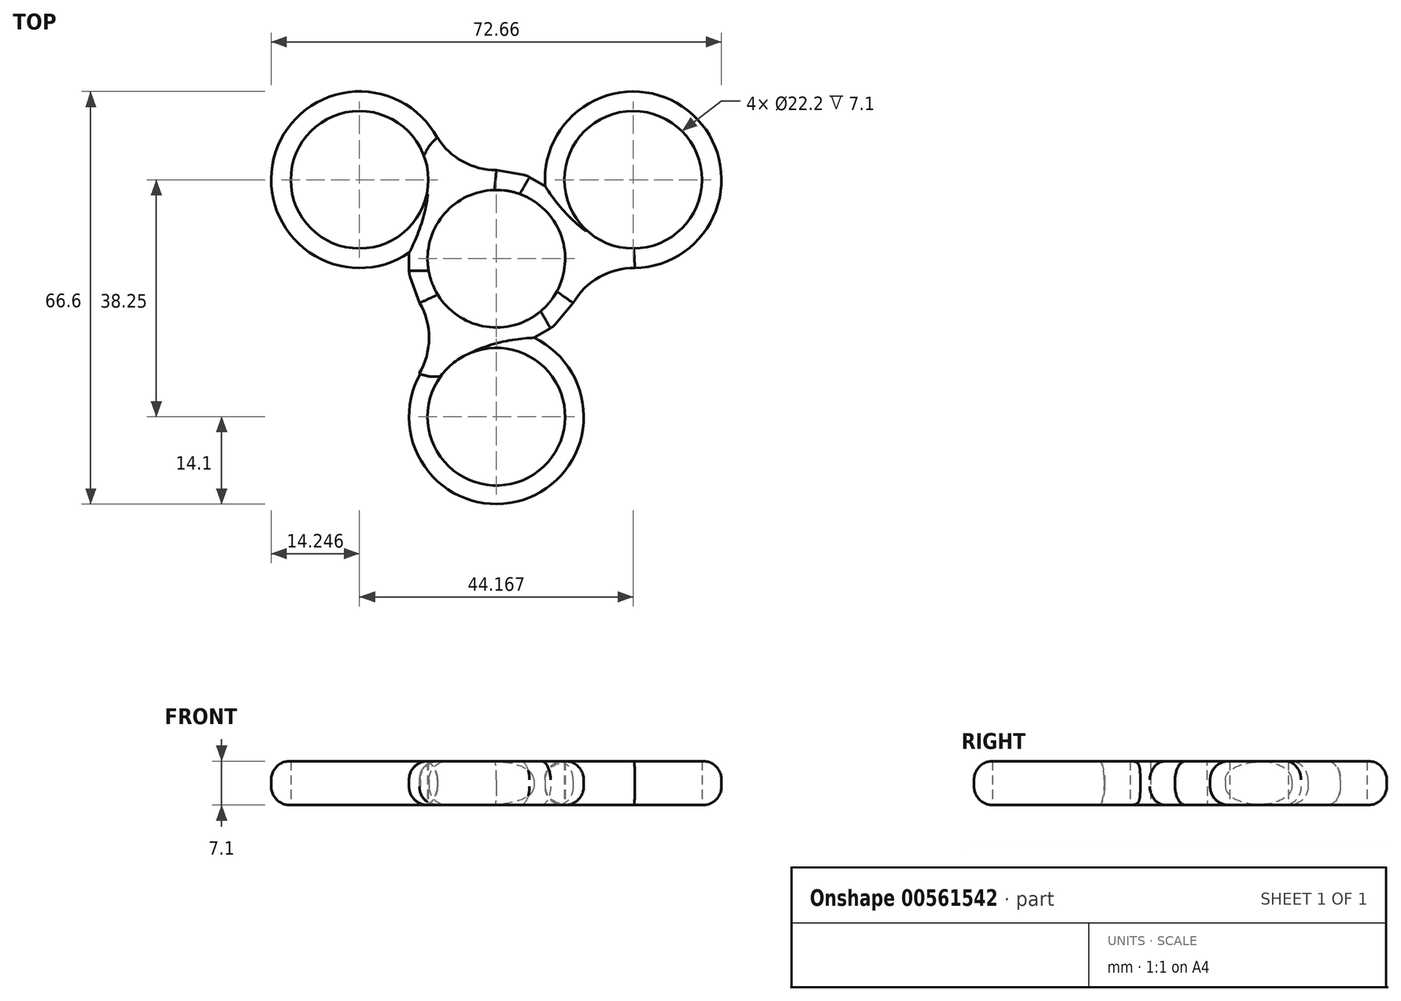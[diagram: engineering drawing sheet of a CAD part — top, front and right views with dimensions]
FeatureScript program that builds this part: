
annotation { "Feature Type Name" : "Feature", "Feature Type Description" : "" }
export const myFeature = defineFeature(function(context is Context, id is Id, definition is map)
    precondition{}
    {
        {
            var Q0;
            Q0=qCreatedBy(makeId("Top.planeOp"),FACE);
            var sketch = newSketch(context, id + "F0", { "sketchPlane" : qUnion([Q0])});
            skCircle(sketch, "E0", {"center": v(0, 0) * mm, "radius": 11.1 * mm});
            skCircle(sketch, "E1.cCircle", {"center": v(0, 0) * mm, "radius": 14.08 * mm, "construction": true});
            skLineSegment(sketch, "E1.0", {"start": v(14.08, 2.48) * mm, "end": v(14.08, -2.48) * mm});
            skLineSegment(sketch, "E1.1", {"start": v(14.08, -2.48) * mm, "end": v(12.38, -7.15) * mm});
            skLineSegment(sketch, "E1.2", {"start": v(12.38, -7.15) * mm, "end": v(9.2, -10.95) * mm});
            skLineSegment(sketch, "E1.3", {"start": v(9.2, -10.95) * mm, "end": v(4.9, -13.44) * mm});
            skLineSegment(sketch, "E1.4", {"start": v(4.9, -13.44) * mm, "end": v(0, -14.3) * mm});
            skLineSegment(sketch, "E1.5", {"start": v(0, -14.3) * mm, "end": v(-4.9, -13.44) * mm});
            skLineSegment(sketch, "E1.6", {"start": v(-4.9, -13.44) * mm, "end": v(-9.2, -10.95) * mm});
            skLineSegment(sketch, "E1.7", {"start": v(-9.2, -10.95) * mm, "end": v(-12.38, -7.15) * mm});
            skLineSegment(sketch, "E1.8", {"start": v(-12.38, -7.15) * mm, "end": v(-14.08, -2.48) * mm});
            skLineSegment(sketch, "E1.9", {"start": v(-14.08, -2.48) * mm, "end": v(-14.08, 2.48) * mm});
            skLineSegment(sketch, "E1.10", {"start": v(-14.08, 2.48) * mm, "end": v(-12.38, 7.15) * mm});
            skLineSegment(sketch, "E1.11", {"start": v(-12.38, 7.15) * mm, "end": v(-9.2, 10.95) * mm});
            skLineSegment(sketch, "E1.12", {"start": v(-9.2, 10.95) * mm, "end": v(-4.9, 13.44) * mm});
            skLineSegment(sketch, "E1.13", {"start": v(-4.9, 13.44) * mm, "end": v(0, 14.3) * mm});
            skLineSegment(sketch, "E1.14", {"start": v(0, 14.3) * mm, "end": v(4.9, 13.44) * mm});
            skLineSegment(sketch, "E1.15", {"start": v(4.9, 13.44) * mm, "end": v(9.2, 10.95) * mm});
            skLineSegment(sketch, "E1.16", {"start": v(9.2, 10.95) * mm, "end": v(12.38, 7.15) * mm});
            skLineSegment(sketch, "E1.17", {"start": v(12.38, 7.15) * mm, "end": v(14.08, 2.48) * mm});
            skPoint(sketch, "E1.0.midPoint", {"position": v(14.08, 0) * mm});
            skLineSegment(sketch, "E2", {"start": v(0, -14.3) * mm, "end": v(0, -25.5) * mm});
            skLineSegment(sketch, "E3", {"start": v(12.38, 7.15) * mm, "end": v(22.08, 12.75) * mm});
            skLineSegment(sketch, "E4", {"start": v(-12.38, 7.15) * mm, "end": v(-22.08, 12.75) * mm});
            skLineSegment(sketch, "E5", {"start": v(0, -25.5) * mm, "end": v(0, -36.25) * mm});
            skLineSegment(sketch, "E6", {"start": v(-22.08, 12.75) * mm, "end": v(-31.44, 18.15) * mm});
            skLineSegment(sketch, "E7", {"start": v(22.08, 12.75) * mm, "end": v(31.92, 18.43) * mm});
            skCircle(sketch, "E8", {"center": v(0, -25.5) * mm, "radius": 11.1 * mm});
            skCircle(sketch, "E9", {"center": v(-22.08, 12.75) * mm, "radius": 11.1 * mm});
            skCircle(sketch, "E10", {"center": v(22.08, 12.75) * mm, "radius": 11.1 * mm});
            skCircle(sketch, "E11.0", {"center": v(-22.08, 12.75) * mm, "radius": 14.25 * mm});
            skCircle(sketch, "E12.0", {"center": v(22.08, 12.75) * mm, "radius": 14.25 * mm});
            skCircle(sketch, "E13.0", {"center": v(0, -25.5) * mm, "radius": 14.1 * mm});
            skLineSegment(sketch, "E14", {"start": v(0, 14.3) * mm, "end": v(0, 25.55) * mm});
            skCircle(sketch, "E15", {"center": v(0, 25.55) * mm, "radius": 11.25 * mm});
            skLineSegment(sketch, "E16", {"start": v(-12.38, -7.15) * mm, "end": v(-22.17, -12.8) * mm});
            skCircle(sketch, "E17", {"center": v(-22.17, -12.8) * mm, "radius": 11.3 * mm});
            skCircle(sketch, "E18", {"center": v(22.17, -12.8) * mm, "radius": 11.3 * mm});
            skCircle(sketch, "E19", {"center": v(15.97, -1.86) * mm, "radius": 6.4 * mm});
            skCircle(sketch, "E20", {"center": v(9.51, -13.38) * mm, "radius": 6.86 * mm});
            skCircle(sketch, "E21", {"center": v(-9.94, -12.85) * mm, "radius": 6.2 * mm});
            skCircle(sketch, "E22", {"center": v(-15.58, -1.28) * mm, "radius": 6.68 * mm});
            skCircle(sketch, "E23", {"center": v(6.28, 14.75) * mm, "radius": 6.3 * mm});
            skPoint(sketch, "E23.second.point", {"position": v(9.78, 20) * mm});
            skPoint(sketch, "E23.third.point", {"position": v(8.83, 9) * mm});
            skCircle(sketch, "E24", {"center": v(-5.99, 14.66) * mm, "radius": 6 * mm});
            skPoint(sketch, "E24.second.point", {"position": v(-9.5, 19.52) * mm});
            skPoint(sketch, "E24.third.point", {"position": v(-8.6, 9.26) * mm});
            skSolve(sketch);
        }
        {
            var Q0;
            {var subQ0=sQuery(id+"F0.wireOp",EDGE,"E20");var subQ1=sQuery(id+"F0.wireOp",EDGE,"E8");var subQ2=makeQuery(id+"F0.imprint","INTERSECT",VERTEX,{"disambiguationData":[OD(1.0)],"derivedFrom":[subQ1,subQ0]});Q0=makeQuery(id+"F0.imprint","IMPRINT",FACE,{"disambiguationData":[TD([[makeQuery(id+"F0.imprint","IMPRINT",EDGE,{"disambiguationData":[TD([[subQ2,1.0]])],"derivedFrom":subQ1}),-1.0]])]});}
            var Q1;
            {var subQ0=sQuery(id+"F0.wireOp",EDGE,"E1.4");var subQ1=sQuery(id+"F0.wireOp",EDGE,"E1.3");var subQ2=makeQuery(id+"F0.imprint","INTERSECT",VERTEX,{"derivedFrom":[subQ1,subQ0]});Q1=makeQuery(id+"F0.imprint","IMPRINT",FACE,{"disambiguationData":[TD([[makeQuery(id+"F0.imprint","IMPRINT",EDGE,{"disambiguationData":[TD([[subQ2,1.0]])],"derivedFrom":subQ1}),1.0]])]});}
            var Q2;
            {var subQ4=sQuery(id+"F0.wireOp",EDGE,"E1.6");var subQ5=sQuery(id+"F0.wireOp",EDGE,"E1.5");var subQ6=makeQuery(id+"F0.imprint","INTERSECT",VERTEX,{"derivedFrom":[subQ5,subQ4]});Q2=makeQuery(id+"F0.imprint","IMPRINT",FACE,{"disambiguationData":[TD([[makeQuery(id+"F0.imprint","IMPRINT",EDGE,{"disambiguationData":[TD([[subQ6,1.0]])],"derivedFrom":subQ5}),1.0]])]});}
            var Q3;
            {var subQ5=sQuery(id+"F0.wireOp",EDGE,"E1.7");Q3=makeQuery(id+"F0.imprint","IMPRINT",FACE,{"disambiguationData":[TD([[makeQuery(id+"F0.imprint","IMPRINT",EDGE,{"derivedFrom":subQ5}),-1.0]])]});}
            var Q4;
            {var subQ9=sQuery(id+"F0.wireOp",EDGE,"E13.0");var subQ11=sQuery(id+"F0.wireOp",EDGE,"E0");var subQ12=makeQuery(id+"F0.imprint","INTERSECT",VERTEX,{"disambiguationData":[OD(0.0)],"derivedFrom":[subQ11,subQ9]});Q4=makeQuery(id+"F0.imprint","IMPRINT",FACE,{"disambiguationData":[TD([[makeQuery(id+"F0.imprint","IMPRINT",EDGE,{"disambiguationData":[TD([[subQ12,-1.0]])],"derivedFrom":subQ11}),-1.0]])]});}
            var Q5;
            {var subQ0=sQuery(id+"F0.wireOp",EDGE,"E1.4");var subQ1=sQuery(id+"F0.wireOp",EDGE,"E1.3");var subQ2=makeQuery(id+"F0.imprint","INTERSECT",VERTEX,{"derivedFrom":[subQ1,subQ0]});Q5=makeQuery(id+"F0.imprint","IMPRINT",FACE,{"disambiguationData":[TD([[makeQuery(id+"F0.imprint","IMPRINT",EDGE,{"disambiguationData":[TD([[subQ2,1.0]])],"derivedFrom":subQ1}),-1.0]])]});}
            var Q6;
            {var subQ0=sQuery(id+"F0.wireOp",EDGE,"E1.6");var subQ1=sQuery(id+"F0.wireOp",EDGE,"E1.5");var subQ2=makeQuery(id+"F0.imprint","INTERSECT",VERTEX,{"derivedFrom":[subQ1,subQ0]});Q6=makeQuery(id+"F0.imprint","IMPRINT",FACE,{"disambiguationData":[TD([[makeQuery(id+"F0.imprint","IMPRINT",EDGE,{"disambiguationData":[TD([[subQ2,1.0]])],"derivedFrom":subQ1}),-1.0]])]});}
            var Q7;
            {var subQ0=sQuery(id+"F0.wireOp",EDGE,"E8");var subQ1=sQuery(id+"F0.wireOp",EDGE,"E1.5");var subQ2=makeQuery(id+"F0.imprint","INTERSECT",VERTEX,{"derivedFrom":[subQ1,subQ0]});Q7=makeQuery(id+"F0.imprint","IMPRINT",FACE,{"disambiguationData":[TD([[makeQuery(id+"F0.imprint","IMPRINT",EDGE,{"disambiguationData":[TD([[subQ2,-1.0]])],"derivedFrom":subQ1}),1.0]])]});}
            var Q8;
            {var subQ0=sQuery(id+"F0.wireOp",EDGE,"E20");var subQ1=sQuery(id+"F0.wireOp",EDGE,"E1.4");var subQ2=makeQuery(id+"F0.imprint","INTERSECT",VERTEX,{"derivedFrom":[subQ1,subQ0]});Q8=makeQuery(id+"F0.imprint","IMPRINT",FACE,{"disambiguationData":[TD([[makeQuery(id+"F0.imprint","IMPRINT",EDGE,{"disambiguationData":[TD([[subQ2,-1.0]])],"derivedFrom":subQ1}),1.0]])]});}
            var Q9;
            {var subQ0=sQuery(id+"F0.wireOp",EDGE,"E13.0");var subQ1=sQuery(id+"F0.wireOp",EDGE,"E0");var subQ2=makeQuery(id+"F0.imprint","INTERSECT",VERTEX,{"disambiguationData":[OD(1.0)],"derivedFrom":[subQ1,subQ0]});Q9=makeQuery(id+"F0.imprint","IMPRINT",FACE,{"disambiguationData":[TD([[makeQuery(id+"F0.imprint","IMPRINT",EDGE,{"disambiguationData":[TD([[subQ2,-1.0]])],"derivedFrom":subQ1}),-1.0]])]});}
            var Q10;
            {var subQ0=sQuery(id+"F0.wireOp",EDGE,"E21");var subQ1=sQuery(id+"F0.wireOp",EDGE,"E0");var subQ2=makeQuery(id+"F0.imprint","INTERSECT",VERTEX,{"disambiguationData":[OD(1.0)],"derivedFrom":[subQ1,subQ0]});Q10=makeQuery(id+"F0.imprint","IMPRINT",FACE,{"disambiguationData":[TD([[makeQuery(id+"F0.imprint","IMPRINT",EDGE,{"disambiguationData":[TD([[subQ2,-1.0]])],"derivedFrom":subQ1}),-1.0]])]});}
            var Q11;
            {var subQ0=sQuery(id+"F0.wireOp",EDGE,"E22");var subQ1=sQuery(id+"F0.wireOp",EDGE,"E0");var subQ2=makeQuery(id+"F0.imprint","INTERSECT",VERTEX,{"disambiguationData":[OD(1.0)],"derivedFrom":[subQ1,subQ0]});Q11=makeQuery(id+"F0.imprint","IMPRINT",FACE,{"disambiguationData":[TD([[makeQuery(id+"F0.imprint","IMPRINT",EDGE,{"disambiguationData":[TD([[subQ2,-1.0]])],"derivedFrom":subQ1}),-1.0]])]});}
            var Q12;
            {var subQ0=sQuery(id+"F0.wireOp",EDGE,"E1.8");Q12=makeQuery(id+"F0.imprint","IMPRINT",FACE,{"disambiguationData":[TD([[makeQuery(id+"F0.imprint","IMPRINT",EDGE,{"derivedFrom":subQ0}),-1.0]])]});}
            var Q13;
            {var subQ0=sQuery(id+"F0.wireOp",EDGE,"E1.10");var subQ1=sQuery(id+"F0.wireOp",EDGE,"E1.9");var subQ2=makeQuery(id+"F0.imprint","INTERSECT",VERTEX,{"derivedFrom":[subQ1,subQ0]});Q13=makeQuery(id+"F0.imprint","IMPRINT",FACE,{"disambiguationData":[TD([[makeQuery(id+"F0.imprint","IMPRINT",EDGE,{"disambiguationData":[TD([[subQ2,1.0]])],"derivedFrom":subQ1}),-1.0]])]});}
            var Q14;
            {var subQ5=sQuery(id+"F0.wireOp",EDGE,"E11.0");var subQ6=sQuery(id+"F0.wireOp",EDGE,"E0");var subQ7=makeQuery(id+"F0.imprint","INTERSECT",VERTEX,{"disambiguationData":[OD(0.0)],"derivedFrom":[subQ6,subQ5]});Q14=makeQuery(id+"F0.imprint","IMPRINT",FACE,{"disambiguationData":[TD([[makeQuery(id+"F0.imprint","IMPRINT",EDGE,{"disambiguationData":[TD([[subQ7,-1.0]])],"derivedFrom":subQ6}),-1.0]])]});}
            var Q15;
            {var subQ0=sQuery(id+"F0.wireOp",EDGE,"E11.0");var subQ1=sQuery(id+"F0.wireOp",EDGE,"E0");var subQ2=makeQuery(id+"F0.imprint","INTERSECT",VERTEX,{"disambiguationData":[OD(1.0)],"derivedFrom":[subQ1,subQ0]});Q15=makeQuery(id+"F0.imprint","IMPRINT",FACE,{"disambiguationData":[TD([[makeQuery(id+"F0.imprint","IMPRINT",EDGE,{"disambiguationData":[TD([[subQ2,-1.0]])],"derivedFrom":subQ1}),-1.0]])]});}
            var Q16;
            {var subQ0=sQuery(id+"F0.wireOp",EDGE,"E9");var subQ1=sQuery(id+"F0.wireOp",EDGE,"E1.11");var subQ2=makeQuery(id+"F0.imprint","INTERSECT",VERTEX,{"derivedFrom":[subQ1,subQ0]});Q16=makeQuery(id+"F0.imprint","IMPRINT",FACE,{"disambiguationData":[TD([[makeQuery(id+"F0.imprint","IMPRINT",EDGE,{"disambiguationData":[TD([[subQ2,-1.0]])],"derivedFrom":subQ1}),1.0]])]});}
            var Q17;
            {var subQ3=sQuery(id+"F0.wireOp",EDGE,"E1.12");var subQ8=sQuery(id+"F0.wireOp",EDGE,"E1.11");var subQ9=makeQuery(id+"F0.imprint","INTERSECT",VERTEX,{"derivedFrom":[subQ8,subQ3]});Q17=makeQuery(id+"F0.imprint","IMPRINT",FACE,{"disambiguationData":[TD([[makeQuery(id+"F0.imprint","IMPRINT",EDGE,{"disambiguationData":[TD([[subQ9,1.0]])],"derivedFrom":subQ8}),1.0]])]});}
            var Q18;
            {var subQ0=sQuery(id+"F0.wireOp",EDGE,"E1.12");var subQ1=sQuery(id+"F0.wireOp",EDGE,"E1.11");var subQ2=makeQuery(id+"F0.imprint","INTERSECT",VERTEX,{"derivedFrom":[subQ1,subQ0]});Q18=makeQuery(id+"F0.imprint","IMPRINT",FACE,{"disambiguationData":[TD([[makeQuery(id+"F0.imprint","IMPRINT",EDGE,{"disambiguationData":[TD([[subQ2,1.0]])],"derivedFrom":subQ1}),-1.0]])]});}
            var Q19;
            {var subQ3=sQuery(id+"F0.wireOp",EDGE,"cm5j0aGU-gvt7-gmux-ldm7-LsrrXDcJTnSL");var subQ9=sQuery(id+"F0.wireOp",EDGE,"E0");var subQ10=makeQuery(id+"F0.imprint","INTERSECT",VERTEX,{"disambiguationData":[OD(1.0)],"derivedFrom":[subQ9,subQ3]});Q19=makeQuery(id+"F0.imprint","IMPRINT",FACE,{"disambiguationData":[TD([[makeQuery(id+"F0.imprint","IMPRINT",EDGE,{"disambiguationData":[TD([[subQ10,-1.0]])],"derivedFrom":subQ9}),-1.0]])]});}
            var Q20;
            {var subQ0=sQuery(id+"F0.wireOp",EDGE,"E22");var subQ1=sQuery(id+"F0.wireOp",EDGE,"E9");var subQ2=makeQuery(id+"F0.imprint","INTERSECT",VERTEX,{"disambiguationData":[OD(0.0)],"derivedFrom":[subQ1,subQ0]});Q20=makeQuery(id+"F0.imprint","IMPRINT",FACE,{"disambiguationData":[TD([[makeQuery(id+"F0.imprint","IMPRINT",EDGE,{"disambiguationData":[TD([[subQ2,1.0]])],"derivedFrom":subQ1}),-1.0]])]});}
            var Q21;
            {var subQ3=sQuery(id+"F0.wireOp",EDGE,"E10");var subQ7=makeQuery(id+"F0.imprint","INTERSECT",VERTEX,{"derivedFrom":[sQuery(id+"F0.wireOp",EDGE,"E7"),subQ3]});Q21=makeQuery(id+"F0.imprint","IMPRINT",FACE,{"disambiguationData":[TD([[makeQuery(id+"F0.imprint","IMPRINT",EDGE,{"disambiguationData":[TD([[subQ7,-1.0]])],"derivedFrom":subQ3}),-1.0]])]});}
            var Q22;
            {var subQ3=sQuery(id+"F0.wireOp",EDGE,"E1.9");var subQ5=sQuery(id+"F0.wireOp",EDGE,"E1.10");var subQ6=makeQuery(id+"F0.imprint","INTERSECT",VERTEX,{"derivedFrom":[subQ3,subQ5]});Q22=makeQuery(id+"F0.imprint","IMPRINT",FACE,{"disambiguationData":[TD([[makeQuery(id+"F0.imprint","IMPRINT",EDGE,{"disambiguationData":[TD([[subQ6,1.0]])],"derivedFrom":subQ3}),1.0]])]});}
            var Q23;
            {var subQ0=sQuery(id+"F0.wireOp",EDGE,"45i7NtGA-5T9x-fNug-wwwZ-XPUVxcpOkaTa");var subQ1=sQuery(id+"F0.wireOp",EDGE,"E0");var subQ2=makeQuery(id+"F0.imprint","INTERSECT",VERTEX,{"disambiguationData":[OD(1.0)],"derivedFrom":[subQ1,subQ0]});Q23=makeQuery(id+"F0.imprint","IMPRINT",FACE,{"disambiguationData":[TD([[makeQuery(id+"F0.imprint","IMPRINT",EDGE,{"disambiguationData":[TD([[subQ2,-1.0]])],"derivedFrom":subQ1}),-1.0]])]});}
            var Q24;
            {var subQ0=sQuery(id+"F0.wireOp",EDGE,"E22");var subQ1=sQuery(id+"F0.wireOp",EDGE,"E1.10");var subQ2=makeQuery(id+"F0.imprint","INTERSECT",VERTEX,{"derivedFrom":[subQ1,subQ0]});Q24=makeQuery(id+"F0.imprint","IMPRINT",FACE,{"disambiguationData":[TD([[makeQuery(id+"F0.imprint","IMPRINT",EDGE,{"disambiguationData":[TD([[subQ2,-1.0]])],"derivedFrom":subQ1}),1.0]])]});}
            var Q25;
            {var subQ4=sQuery(id+"F0.wireOp",EDGE,"E1.16");var subQ5=sQuery(id+"F0.wireOp",EDGE,"E1.15");var subQ6=makeQuery(id+"F0.imprint","INTERSECT",VERTEX,{"derivedFrom":[subQ5,subQ4]});Q25=makeQuery(id+"F0.imprint","IMPRINT",FACE,{"disambiguationData":[TD([[makeQuery(id+"F0.imprint","IMPRINT",EDGE,{"disambiguationData":[TD([[subQ6,1.0]])],"derivedFrom":subQ5}),1.0]])]});}
            var Q26;
            {var subQ3=sQuery(id+"F0.wireOp",EDGE,"cm5j0aGU-gvt7-gmux-ldm7-LsrrXDcJTnSL");var subQ9=sQuery(id+"F0.wireOp",EDGE,"E0");var subQ10=makeQuery(id+"F0.imprint","INTERSECT",VERTEX,{"disambiguationData":[OD(0.0)],"derivedFrom":[subQ9,subQ3]});Q26=makeQuery(id+"F0.imprint","IMPRINT",FACE,{"disambiguationData":[TD([[makeQuery(id+"F0.imprint","IMPRINT",EDGE,{"disambiguationData":[TD([[subQ10,-1.0]])],"derivedFrom":subQ9}),-1.0]])]});}
            var Q27;
            {var subQ3=sQuery(id+"F0.wireOp",EDGE,"45i7NtGA-5T9x-fNug-wwwZ-XPUVxcpOkaTa");var subQ6=sQuery(id+"F0.wireOp",EDGE,"E0");var subQ9=makeQuery(id+"F0.imprint","INTERSECT",VERTEX,{"disambiguationData":[OD(0.0)],"derivedFrom":[subQ6,subQ3]});Q27=makeQuery(id+"F0.imprint","IMPRINT",FACE,{"disambiguationData":[TD([[makeQuery(id+"F0.imprint","IMPRINT",EDGE,{"disambiguationData":[TD([[subQ9,-1.0]])],"derivedFrom":subQ6}),-1.0]])]});}
            var Q28;
            {var subQ1=sQuery(id+"F0.wireOp",EDGE,"E1.13");var subQ3=sQuery(id+"F0.wireOp",EDGE,"cm5j0aGU-gvt7-gmux-ldm7-LsrrXDcJTnSL");var subQ4=makeQuery(id+"F0.imprint","INTERSECT",VERTEX,{"derivedFrom":[subQ1,subQ3]});Q28=makeQuery(id+"F0.imprint","IMPRINT",FACE,{"disambiguationData":[TD([[makeQuery(id+"F0.imprint","IMPRINT",EDGE,{"disambiguationData":[TD([[subQ4,1.0]])],"derivedFrom":subQ3}),1.0]])]});}
            var Q29;
            {var subQ1=sQuery(id+"F0.wireOp",EDGE,"E1.14");var subQ3=sQuery(id+"F0.wireOp",EDGE,"45i7NtGA-5T9x-fNug-wwwZ-XPUVxcpOkaTa");var subQ4=makeQuery(id+"F0.imprint","INTERSECT",VERTEX,{"derivedFrom":[subQ1,subQ3]});Q29=makeQuery(id+"F0.imprint","IMPRINT",FACE,{"disambiguationData":[TD([[makeQuery(id+"F0.imprint","IMPRINT",EDGE,{"disambiguationData":[TD([[subQ4,-1.0]])],"derivedFrom":subQ3}),1.0]])]});}
            var Q30;
            {var subQ0=sQuery(id+"F0.wireOp",EDGE,"cm5j0aGU-gvt7-gmux-ldm7-LsrrXDcJTnSL");var subQ1=sQuery(id+"F0.wireOp",EDGE,"E1.16");var subQ2=makeQuery(id+"F0.imprint","INTERSECT",VERTEX,{"derivedFrom":[subQ1,subQ0]});Q30=makeQuery(id+"F0.imprint","IMPRINT",FACE,{"disambiguationData":[TD([[makeQuery(id+"F0.imprint","IMPRINT",EDGE,{"disambiguationData":[TD([[subQ2,-1.0]])],"derivedFrom":subQ1}),1.0]])]});}
            var Q31;
            {var subQ0=sQuery(id+"F0.wireOp",EDGE,"E12.0");var subQ1=sQuery(id+"F0.wireOp",EDGE,"E0");var subQ2=makeQuery(id+"F0.imprint","INTERSECT",VERTEX,{"disambiguationData":[OD(1.0)],"derivedFrom":[subQ1,subQ0]});Q31=makeQuery(id+"F0.imprint","IMPRINT",FACE,{"disambiguationData":[TD([[makeQuery(id+"F0.imprint","IMPRINT",EDGE,{"disambiguationData":[TD([[subQ2,-1.0]])],"derivedFrom":subQ1}),-1.0]])]});}
            var Q32;
            {var subQ9=sQuery(id+"F0.wireOp",EDGE,"E12.0");var subQ10=sQuery(id+"F0.wireOp",EDGE,"E0");var subQ13=makeQuery(id+"F0.imprint","INTERSECT",VERTEX,{"disambiguationData":[OD(0.0)],"derivedFrom":[subQ10,subQ9]});Q32=makeQuery(id+"F0.imprint","IMPRINT",FACE,{"disambiguationData":[TD([[makeQuery(id+"F0.imprint","IMPRINT",EDGE,{"disambiguationData":[TD([[subQ13,-1.0]])],"derivedFrom":subQ10}),-1.0]])]});}
            var Q33;
            {var subQ0=sQuery(id+"F0.wireOp",EDGE,"E12.0");var subQ1=sQuery(id+"F0.wireOp",EDGE,"E0");var subQ2=makeQuery(id+"F0.imprint","INTERSECT",VERTEX,{"disambiguationData":[OD(0.0)],"derivedFrom":[subQ1,subQ0]});Q33=makeQuery(id+"F0.imprint","IMPRINT",FACE,{"disambiguationData":[TD([[makeQuery(id+"F0.imprint","IMPRINT",EDGE,{"disambiguationData":[TD([[subQ2,1.0]])],"derivedFrom":subQ1}),-1.0]])]});}
            var Q34;
            {var subQ0=sQuery(id+"F0.wireOp",EDGE,"E1.17");var subQ1=sQuery(id+"F0.wireOp",EDGE,"E1.0");var subQ2=makeQuery(id+"F0.imprint","INTERSECT",VERTEX,{"derivedFrom":[subQ1,subQ0]});Q34=makeQuery(id+"F0.imprint","IMPRINT",FACE,{"disambiguationData":[TD([[makeQuery(id+"F0.imprint","IMPRINT",EDGE,{"disambiguationData":[TD([[subQ2,-1.0]])],"derivedFrom":subQ1}),-1.0]])]});}
            var Q35;
            {var subQ5=sQuery(id+"F0.wireOp",EDGE,"E1.1");Q35=makeQuery(id+"F0.imprint","IMPRINT",FACE,{"disambiguationData":[TD([[makeQuery(id+"F0.imprint","IMPRINT",EDGE,{"derivedFrom":subQ5}),-1.0]])]});}
            var Q36;
            {var subQ0=sQuery(id+"F0.wireOp",EDGE,"E20");var subQ1=sQuery(id+"F0.wireOp",EDGE,"E0");var subQ2=makeQuery(id+"F0.imprint","INTERSECT",VERTEX,{"disambiguationData":[OD(1.0)],"derivedFrom":[subQ1,subQ0]});Q36=makeQuery(id+"F0.imprint","IMPRINT",FACE,{"disambiguationData":[TD([[makeQuery(id+"F0.imprint","IMPRINT",EDGE,{"disambiguationData":[TD([[subQ2,-1.0]])],"derivedFrom":subQ1}),-1.0]])]});}
            var Q37;
            {var subQ5=sQuery(id+"F0.wireOp",EDGE,"E1.2");Q37=makeQuery(id+"F0.imprint","IMPRINT",FACE,{"disambiguationData":[TD([[makeQuery(id+"F0.imprint","IMPRINT",EDGE,{"derivedFrom":subQ5}),-1.0]])]});}
            var Q38;
            {var subQ0=sQuery(id+"F0.wireOp",EDGE,"E1.16");var subQ1=sQuery(id+"F0.wireOp",EDGE,"E1.15");var subQ2=makeQuery(id+"F0.imprint","INTERSECT",VERTEX,{"derivedFrom":[subQ1,subQ0]});Q38=makeQuery(id+"F0.imprint","IMPRINT",FACE,{"disambiguationData":[TD([[makeQuery(id+"F0.imprint","IMPRINT",EDGE,{"disambiguationData":[TD([[subQ2,1.0]])],"derivedFrom":subQ1}),-1.0]])]});}
            var Q39;
            {var subQ3=sQuery(id+"F0.wireOp",EDGE,"E1.0");var subQ8=sQuery(id+"F0.wireOp",EDGE,"E1.17");var subQ9=makeQuery(id+"F0.imprint","INTERSECT",VERTEX,{"derivedFrom":[subQ3,subQ8]});Q39=makeQuery(id+"F0.imprint","IMPRINT",FACE,{"disambiguationData":[TD([[makeQuery(id+"F0.imprint","IMPRINT",EDGE,{"disambiguationData":[TD([[subQ9,-1.0]])],"derivedFrom":subQ3}),1.0]])]});}
            var Q40;
            {var subQ0=sQuery(id+"F0.wireOp",EDGE,"E10");var subQ1=sQuery(id+"F0.wireOp",EDGE,"E1.17");var subQ2=makeQuery(id+"F0.imprint","INTERSECT",VERTEX,{"derivedFrom":[subQ1,subQ0]});Q40=makeQuery(id+"F0.imprint","IMPRINT",FACE,{"disambiguationData":[TD([[makeQuery(id+"F0.imprint","IMPRINT",EDGE,{"disambiguationData":[TD([[subQ2,-1.0]])],"derivedFrom":subQ1}),1.0]])]});}
            var Q41;
            {var subQ2=sQuery(id+"F0.wireOp",EDGE,"E1.1");Q41=makeQuery(id+"F0.imprint","IMPRINT",FACE,{"disambiguationData":[TD([[makeQuery(id+"F0.imprint","IMPRINT",EDGE,{"derivedFrom":subQ2}),1.0]])]});}
            var Q42;
            {var subQ3=sQuery(id+"F0.wireOp",EDGE,"E1.12");var subQ7=sQuery(id+"F0.wireOp",EDGE,"E1.13");var subQ8=makeQuery(id+"F0.imprint","INTERSECT",VERTEX,{"derivedFrom":[subQ3,subQ7]});Q42=makeQuery(id+"F0.imprint","IMPRINT",FACE,{"disambiguationData":[TD([[makeQuery(id+"F0.imprint","IMPRINT",EDGE,{"disambiguationData":[TD([[subQ8,1.0]])],"derivedFrom":subQ3}),1.0]])]});}
            var Q43;
            {var subQ5=sQuery(id+"F0.wireOp",EDGE,"E1.7");Q43=makeQuery(id+"F0.imprint","IMPRINT",FACE,{"disambiguationData":[TD([[makeQuery(id+"F0.imprint","IMPRINT",EDGE,{"derivedFrom":subQ5}),1.0]])]});}
            var Q44;
            {var subQ5=sQuery(id+"F0.wireOp",EDGE,"E1.14");Q44=makeQuery(id+"F0.imprint","IMPRINT",FACE,{"disambiguationData":[TD([[makeQuery(id+"F0.imprint","IMPRINT",EDGE,{"derivedFrom":subQ5}),-1.0]])]});}
            var Q45;
            {var subQ5=sQuery(id+"F0.wireOp",EDGE,"E1.13");Q45=makeQuery(id+"F0.imprint","IMPRINT",FACE,{"disambiguationData":[TD([[makeQuery(id+"F0.imprint","IMPRINT",EDGE,{"derivedFrom":subQ5}),-1.0]])]});}
            var Q46;
            {var subQ0=sQuery(id+"F0.wireOp",EDGE,"E23");var subQ1=sQuery(id+"F0.wireOp",EDGE,"E0");var subQ2=makeQuery(id+"F0.imprint","INTERSECT",VERTEX,{"disambiguationData":[OD(1.0)],"derivedFrom":[subQ1,subQ0]});Q46=makeQuery(id+"F0.imprint","IMPRINT",FACE,{"disambiguationData":[TD([[makeQuery(id+"F0.imprint","IMPRINT",EDGE,{"disambiguationData":[TD([[subQ2,-1.0]])],"derivedFrom":subQ1}),-1.0]])]});}
            var Q47;
            {var subQ0=sQuery(id+"F0.wireOp",EDGE,"E24");var subQ1=sQuery(id+"F0.wireOp",EDGE,"E0");var subQ2=makeQuery(id+"F0.imprint","INTERSECT",VERTEX,{"disambiguationData":[OD(1.0)],"derivedFrom":[subQ1,subQ0]});Q47=makeQuery(id+"F0.imprint","IMPRINT",FACE,{"disambiguationData":[TD([[makeQuery(id+"F0.imprint","IMPRINT",EDGE,{"disambiguationData":[TD([[subQ2,-1.0]])],"derivedFrom":subQ1}),-1.0]])]});}
            var Q48;
            {var subQ0=sQuery(id+"F0.wireOp",EDGE,"E4");var subQ5=sQuery(id+"F0.wireOp",EDGE,"E9");var subQ6=makeQuery(id+"F0.imprint","INTERSECT",VERTEX,{"derivedFrom":[subQ0,subQ5]});Q48=makeQuery(id+"F0.imprint","IMPRINT",FACE,{"disambiguationData":[TD([[makeQuery(id+"F0.imprint","IMPRINT",EDGE,{"disambiguationData":[TD([[subQ6,-1.0]])],"derivedFrom":subQ5}),-1.0]])]});}
            var Q49;
            {var subQ0=sQuery(id+"F0.wireOp",EDGE,"E22");var subQ1=sQuery(id+"F0.wireOp",EDGE,"E11.0");var subQ2=makeQuery(id+"F0.imprint","INTERSECT",VERTEX,{"disambiguationData":[OD(1.0)],"derivedFrom":[subQ1,subQ0]});Q49=makeQuery(id+"F0.imprint","IMPRINT",FACE,{"disambiguationData":[TD([[makeQuery(id+"F0.imprint","IMPRINT",EDGE,{"disambiguationData":[TD([[subQ2,-1.0]])],"derivedFrom":subQ1}),1.0]])]});}
            var Q50;
            {var subQ3=sQuery(id+"F0.wireOp",EDGE,"E12.0");var subQ5=sQuery(id+"F0.wireOp",EDGE,"E23");var subQ6=makeQuery(id+"F0.imprint","INTERSECT",VERTEX,{"disambiguationData":[OD(1.0)],"derivedFrom":[subQ3,subQ5]});Q50=makeQuery(id+"F0.imprint","IMPRINT",FACE,{"disambiguationData":[TD([[makeQuery(id+"F0.imprint","IMPRINT",EDGE,{"disambiguationData":[TD([[subQ6,-1.0]])],"derivedFrom":subQ3}),1.0]])]});}
            var Q51;
            {var subQ0=sQuery(id+"F0.wireOp",EDGE,"E23");var subQ1=sQuery(id+"F0.wireOp",EDGE,"E0");var subQ2=makeQuery(id+"F0.imprint","INTERSECT",VERTEX,{"disambiguationData":[OD(0.0)],"derivedFrom":[subQ1,subQ0]});Q51=makeQuery(id+"F0.imprint","IMPRINT",FACE,{"disambiguationData":[TD([[makeQuery(id+"F0.imprint","IMPRINT",EDGE,{"disambiguationData":[TD([[subQ2,1.0]])],"derivedFrom":subQ1}),-1.0]])]});}
            var Q52;
            {var subQ0=sQuery(id+"F0.wireOp",EDGE,"E3");var subQ5=sQuery(id+"F0.wireOp",EDGE,"E10");var subQ6=makeQuery(id+"F0.imprint","INTERSECT",VERTEX,{"derivedFrom":[subQ0,subQ5]});Q52=makeQuery(id+"F0.imprint","IMPRINT",FACE,{"disambiguationData":[TD([[makeQuery(id+"F0.imprint","IMPRINT",EDGE,{"disambiguationData":[TD([[subQ6,-1.0]])],"derivedFrom":subQ5}),-1.0]])]});}
            var Q53;
            {var subQ0=sQuery(id+"F0.wireOp",EDGE,"E20");var subQ3=sQuery(id+"F0.wireOp",EDGE,"E13.0");var subQ4=makeQuery(id+"F0.imprint","INTERSECT",VERTEX,{"disambiguationData":[OD(1.0)],"derivedFrom":[subQ3,subQ0]});Q53=makeQuery(id+"F0.imprint","IMPRINT",FACE,{"disambiguationData":[TD([[makeQuery(id+"F0.imprint","IMPRINT",EDGE,{"disambiguationData":[TD([[subQ4,-1.0]])],"derivedFrom":subQ3}),1.0]])]});}
            var Q54;
            {var subQ0=sQuery(id+"F0.wireOp",EDGE,"E2");var subQ5=sQuery(id+"F0.wireOp",EDGE,"E8");var subQ6=makeQuery(id+"F0.imprint","INTERSECT",VERTEX,{"derivedFrom":[subQ0,subQ5]});Q54=makeQuery(id+"F0.imprint","IMPRINT",FACE,{"disambiguationData":[TD([[makeQuery(id+"F0.imprint","IMPRINT",EDGE,{"disambiguationData":[TD([[subQ6,-1.0]])],"derivedFrom":subQ5}),-1.0]])]});}
            extrude(context, id + "F1", {"entities" : qUnion([Q0, Q1, Q2, Q3, Q4, Q5, Q6, Q7, Q8, Q9, Q10, Q11, Q12, Q13, Q14, Q15, Q16, Q17, Q18, Q19, Q20, Q21, Q22, Q23, Q24, Q25, Q26, Q27, Q28, Q29, Q30, Q31, Q32, Q33, Q34, Q35, Q36, Q37, Q38, Q39, Q40, Q41, Q42, Q43, Q44, Q45, Q46, Q47, Q48, Q49, Q50, Q51, Q52, Q53, Q54]), "depth" : 7.1 * mm, "offsetDistance" : 25 * mm});
        }
        {
            var Q0;
            Q0=makeQuery(id+"F1.opExtrude","CAP_EDGE",EDGE,{"disambiguationData":[OSD([sQuery(id+"F0.wireOp",EDGE,"E12.0")])],"isStart":false});
            var Q1;
            Q1=makeQuery(id+"F1.opExtrude","CAP_EDGE",EDGE,{"disambiguationData":[OSD([sQuery(id+"F0.wireOp",EDGE,"E13.0")])],"isStart":false});
            var Q2;
            Q2=makeQuery(id+"F1.opExtrude","CAP_EDGE",EDGE,{"disambiguationData":[OSD([sQuery(id+"F0.wireOp",EDGE,"E11.0")])],"isStart":false});
            var Q3;
            Q3=makeQuery(id+"F1.opExtrude","CAP_EDGE",EDGE,{"disambiguationData":[OSD([sQuery(id+"F0.wireOp",EDGE,"E11.0")])],"isStart":true});
            var Q4;
            Q4=makeQuery(id+"F1.opExtrude","CAP_EDGE",EDGE,{"disambiguationData":[OSD([sQuery(id+"F0.wireOp",EDGE,"E13.0")])],"isStart":true});
            var Q5;
            Q5=makeQuery(id+"F1.opExtrude","CAP_EDGE",EDGE,{"disambiguationData":[OSD([sQuery(id+"F0.wireOp",EDGE,"E12.0")])],"isStart":true});
            var Q6;
            Q6=makeQuery(id+"F1.opExtrude","CAP_EDGE",EDGE,{"disambiguationData":[OSD([sQuery(id+"F0.wireOp",EDGE,"E1.3")])],"isStart":false});
            var Q7;
            Q7=makeQuery(id+"F1.opExtrude","CAP_EDGE",EDGE,{"disambiguationData":[OSD([sQuery(id+"F0.wireOp",EDGE,"E1.9")])],"isStart":false});
            var Q8;
            Q8=makeQuery(id+"F1.opExtrude","CAP_EDGE",EDGE,{"disambiguationData":[OSD([sQuery(id+"F0.wireOp",EDGE,"E1.15")])],"isStart":false});
            var Q9;
            Q9=makeQuery(id+"F1.opExtrude","CAP_EDGE",EDGE,{"disambiguationData":[OSD([sQuery(id+"F0.wireOp",EDGE,"E1.15")])],"isStart":true});
            var Q10;
            Q10=makeQuery(id+"F1.opExtrude","CAP_EDGE",EDGE,{"disambiguationData":[OSD([sQuery(id+"F0.wireOp",EDGE,"E1.9")])],"isStart":true});
            var Q11;
            Q11=makeQuery(id+"F1.opExtrude","CAP_EDGE",EDGE,{"disambiguationData":[OSD([sQuery(id+"F0.wireOp",EDGE,"E1.3")])],"isStart":true});
            fillet(context, id + "F2", {"entities" : qUnion([Q0, Q1, Q2, Q3, Q4, Q5, Q6, Q7, Q8, Q9, Q10, Q11]), "radius" : 3 * mm, "tangentPropagation" : true, "allowEdgeOverflow" : false});
        }
        {
            var Q0;
            Q0=makeQuery(id+"F1.opExtrude","CAP_EDGE",EDGE,{"disambiguationData":[OSD([sQuery(id+"F0.wireOp",EDGE,"E18")])],"isStart":true});
            var Q1;
            Q1=makeQuery(id+"F1.opExtrude","CAP_EDGE",EDGE,{"disambiguationData":[OSD([sQuery(id+"F0.wireOp",EDGE,"E18")])],"isStart":false});
            var Q2;
            Q2=makeQuery(id+"F2.opFillet","BLEND_EDGE",EDGE,{"blendedFrom":[makeQuery(id+"F1.opExtrude","CAP_EDGE",EDGE,{"disambiguationData":[OSD([sQuery(id+"F0.wireOp",EDGE,"E1.3")])],"isStart":false}),makeQuery(id+"F1.opExtrude","SWEPT_FACE",FACE,{"disambiguationData":[OSD([sQuery(id+"F0.wireOp",EDGE,"E1.2")])]})],"blendedInto":[makeQuery(id+"F1.opExtrude","SWEPT_FACE",FACE,{"disambiguationData":[OSD([sQuery(id+"F0.wireOp",EDGE,"E1.2")])]})]});
            var Q3;
            Q3=makeQuery(id+"F2.opFillet","BLEND_EDGE",EDGE,{"blendedFrom":[makeQuery(id+"F1.opExtrude","CAP_EDGE",EDGE,{"disambiguationData":[OSD([sQuery(id+"F0.wireOp",EDGE,"E1.3")])],"isStart":true}),makeQuery(id+"F1.opExtrude","SWEPT_FACE",FACE,{"disambiguationData":[OSD([sQuery(id+"F0.wireOp",EDGE,"E1.2")])]})],"blendedInto":[makeQuery(id+"F1.opExtrude","SWEPT_FACE",FACE,{"disambiguationData":[OSD([sQuery(id+"F0.wireOp",EDGE,"E1.2")])]})]});
            var Q4;
            Q4=makeQuery(id+"F1.opExtrude","CAP_EDGE",EDGE,{"disambiguationData":[OSD([sQuery(id+"F0.wireOp",EDGE,"E17")])],"isStart":true});
            var Q5;
            Q5=makeQuery(id+"F1.opExtrude","CAP_EDGE",EDGE,{"disambiguationData":[OSD([sQuery(id+"F0.wireOp",EDGE,"E17")])],"isStart":false});
            var Q6;
            Q6=makeQuery(id+"F2.opFillet","BLEND_EDGE",EDGE,{"blendedFrom":[makeQuery(id+"F1.opExtrude","CAP_EDGE",EDGE,{"disambiguationData":[OSD([sQuery(id+"F0.wireOp",EDGE,"E1.9")])],"isStart":false}),makeQuery(id+"F1.opExtrude","SWEPT_FACE",FACE,{"disambiguationData":[OSD([sQuery(id+"F0.wireOp",EDGE,"E1.8")])]})],"blendedInto":[makeQuery(id+"F1.opExtrude","SWEPT_FACE",FACE,{"disambiguationData":[OSD([sQuery(id+"F0.wireOp",EDGE,"E1.8")])]})]});
            var Q7;
            Q7=makeQuery(id+"F2.opFillet","BLEND_EDGE",EDGE,{"blendedFrom":[makeQuery(id+"F1.opExtrude","CAP_EDGE",EDGE,{"disambiguationData":[OSD([sQuery(id+"F0.wireOp",EDGE,"E1.9")])],"isStart":true}),makeQuery(id+"F1.opExtrude","SWEPT_FACE",FACE,{"disambiguationData":[OSD([sQuery(id+"F0.wireOp",EDGE,"E1.8")])]})],"blendedInto":[makeQuery(id+"F1.opExtrude","SWEPT_FACE",FACE,{"disambiguationData":[OSD([sQuery(id+"F0.wireOp",EDGE,"E1.8")])]})]});
            var Q8;
            Q8=makeQuery(id+"F1.opExtrude","CAP_EDGE",EDGE,{"disambiguationData":[OSD([sQuery(id+"F0.wireOp",EDGE,"E15")])],"isStart":true});
            var Q9;
            Q9=makeQuery(id+"F1.opExtrude","CAP_EDGE",EDGE,{"disambiguationData":[OSD([sQuery(id+"F0.wireOp",EDGE,"E15")])],"isStart":false});
            var Q10;
            Q10=makeQuery(id+"F2.opFillet","BLEND_EDGE",EDGE,{"blendedFrom":[makeQuery(id+"F1.opExtrude","CAP_EDGE",EDGE,{"disambiguationData":[OSD([sQuery(id+"F0.wireOp",EDGE,"E1.15")])],"isStart":false}),makeQuery(id+"F1.opExtrude","SWEPT_FACE",FACE,{"disambiguationData":[OSD([sQuery(id+"F0.wireOp",EDGE,"E1.14")])]})],"blendedInto":[makeQuery(id+"F1.opExtrude","SWEPT_FACE",FACE,{"disambiguationData":[OSD([sQuery(id+"F0.wireOp",EDGE,"E1.14")])]})]});
            var Q11;
            Q11=makeQuery(id+"F2.opFillet","BLEND_EDGE",EDGE,{"blendedFrom":[makeQuery(id+"F1.opExtrude","CAP_EDGE",EDGE,{"disambiguationData":[OSD([sQuery(id+"F0.wireOp",EDGE,"E1.15")])],"isStart":true}),makeQuery(id+"F1.opExtrude","SWEPT_FACE",FACE,{"disambiguationData":[OSD([sQuery(id+"F0.wireOp",EDGE,"E1.14")])]})],"blendedInto":[makeQuery(id+"F1.opExtrude","SWEPT_FACE",FACE,{"disambiguationData":[OSD([sQuery(id+"F0.wireOp",EDGE,"E1.14")])]})]});
            fillet(context, id + "F3", {"entities" : qUnion([Q0, Q1, Q2, Q3, Q4, Q5, Q6, Q7, Q8, Q9, Q10, Q11]), "radius" : 3 * mm, "tangentPropagation" : true, "allowEdgeOverflow" : false});
        }
    });
